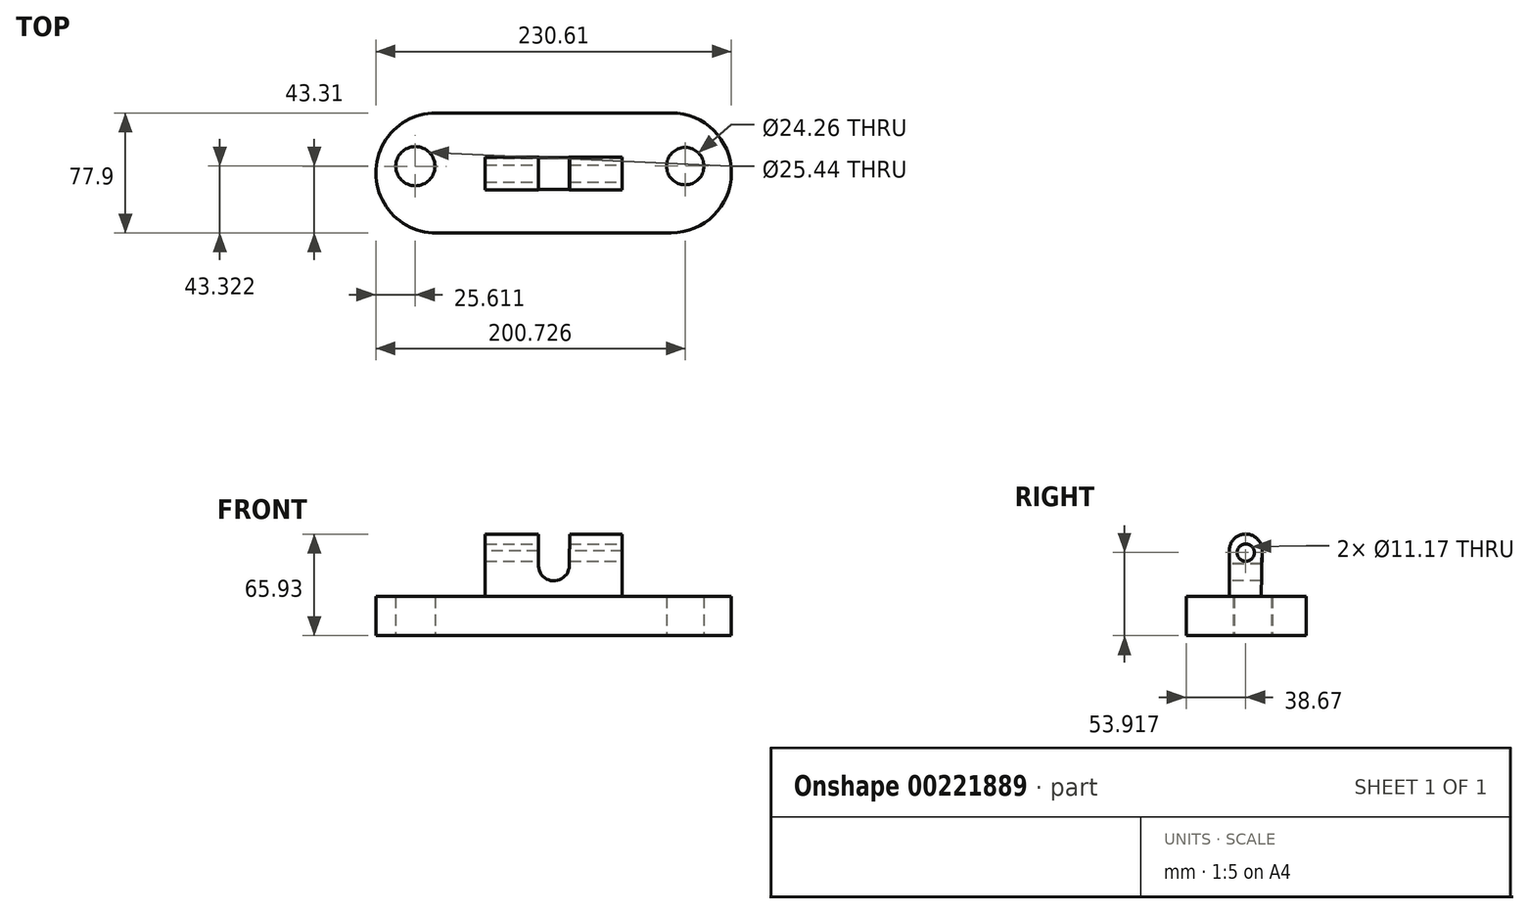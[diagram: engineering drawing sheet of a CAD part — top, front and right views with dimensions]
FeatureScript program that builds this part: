
annotation { "Feature Type Name" : "Feature", "Feature Type Description" : "" }
export const myFeature = defineFeature(function(context is Context, id is Id, definition is map)
    precondition{}
    {
        {
            var Q0;
            Q0=qCreatedBy(makeId("Top.planeOp"),FACE);
            var sketch = newSketch(context, id + "F0", { "sketchPlane" : qUnion([Q0])});
            skLineSegment(sketch, "E0", {"start": v(-76.5, 39.23) * mm, "end": v(76.21, 39.23) * mm});
            skLineSegment(sketch, "E1", {"start": v(-76.21, -38.67) * mm, "end": v(76.21, -38.67) * mm});
            skArc(sketch, "E2", {"start": v(-76.5, 39.23) * mm, "mid": v(-115.45, 0.14) * mm, "end": v(-76.21, -38.67) * mm});
            skArc(sketch, "E3", {"start": v(76.21, 39.23) * mm, "mid": v(115.16, 0.28) * mm, "end": v(76.21, -38.67) * mm});
            skSolve(sketch);
        }
        {
            var Q0;
            Q0 = qSketchRegion(id + "F0", true);
            extrude(context, id + "F1", {"entities" : qUnion([Q0]), "depth" : 25.4 * mm});
        }
        {
            var Q0;
            Q0=qCreatedBy(makeId("Top.planeOp"),FACE);
            var sketch = newSketch(context, id + "F2", { "sketchPlane" : qUnion([Q0])});
            skCircle(sketch, "E4", {"center": v(-89.84, 4.64) * mm, "radius": 12.72 * mm});
            skCircle(sketch, "E5", {"center": v(85.28, 4.65) * mm, "radius": 12.13 * mm});
            skSolve(sketch);
        }
        {
            var Q0;
            Q0 = qSketchRegion(id + "F2", true);
            extrude(context, id + "F3", {"entities" : qUnion([Q0]), "operationType" : NewBodyOperationType.REMOVE, "endBound" : BoundingType.THROUGH_ALL, "depth" : 25.4 * mm});
        }
        {
            var Q0;
            Q0=qCreatedBy(makeId("Right.planeOp"),FACE);
            var sketch = newSketch(context, id + "F4", { "sketchPlane" : qUnion([Q0])});
            skCircle(sketch, "E6", {"center": v(0, 55.3) * mm, "radius": 10.62 * mm});
            skLineSegment(sketch, "E7", {"start": v(-10.62, 55.27) * mm, "end": v(-10.49, 10.97) * mm});
            skLineSegment(sketch, "E8", {"start": v(-10.49, 10.97) * mm, "end": v(9.7, 10.97) * mm});
            skLineSegment(sketch, "E9", {"start": v(9.7, 10.97) * mm, "end": v(10.62, 55.3) * mm});
            skSolve(sketch);
        }
        {
            var Q0;
            Q0 = qSketchRegion(id + "F4", true);
            extrude(context, id + "F5", {"entities" : qUnion([Q0]), "operationType" : NewBodyOperationType.ADD, "depth" : 44.45 * mm, "hasSecondDirection" : true, "secondDirectionOppositeDirection" : true, "secondDirectionDepth" : 44.45 * mm});
        }
        {
            var Q0;
            Q0=qCreatedBy(makeId("Front.planeOp"),FACE);
            var sketch = newSketch(context, id + "F6", { "sketchPlane" : qUnion([Q0])});
            skCircle(sketch, "E10", {"center": v(0, 45.6) * mm, "radius": 10.07 * mm});
            skLineSegment(sketch, "E11", {"start": v(-10.03, 44.7) * mm, "end": v(-10.03, 72.4) * mm});
            skLineSegment(sketch, "E12", {"start": v(-10.03, 72.4) * mm, "end": v(10.5, 72.4) * mm});
            skLineSegment(sketch, "E13", {"start": v(10.5, 72.4) * mm, "end": v(9.93, 43.93) * mm});
            skSolve(sketch);
        }
        {
            var Q0;
            Q0 = qSketchRegion(id + "F6", true);
            extrude(context, id + "F7", {"entities" : qUnion([Q0]), "operationType" : NewBodyOperationType.REMOVE, "oppositeDirection" : true, "depth" : 25.4 * mm, "hasSecondDirection" : true, "secondDirectionOppositeDirection" : false, "secondDirectionDepth" : 25.4 * mm});
        }
        {
            var Q0;
            Q0=qCreatedBy(makeId("Right.planeOp"),FACE);
            var sketch = newSketch(context, id + "F8", { "sketchPlane" : qUnion([Q0])});
            skCircle(sketch, "E14", {"center": v(0, 53.92) * mm, "radius": 5.58 * mm});
            skSolve(sketch);
        }
        {
            var Q0;
            Q0 = qSketchRegion(id + "F8", true);
            extrude(context, id + "F9", {"entities" : qUnion([Q0]), "operationType" : NewBodyOperationType.REMOVE, "endBound" : BoundingType.THROUGH_ALL, "oppositeDirection" : true, "depth" : 25.4 * mm, "hasSecondDirection" : true, "secondDirectionOppositeDirection" : false, "secondDirectionDepth" : 68.58 * mm});
        }
    });
